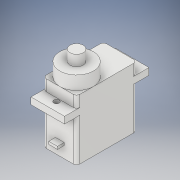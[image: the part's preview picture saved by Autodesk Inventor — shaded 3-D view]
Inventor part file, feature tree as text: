
AUTODESK INVENTOR PART (.ipt)
format: ipt  version: 2018 (Build 220112000, 112)  size: 165,376 bytes
history: native  units: in
note: dims shown in document units (in); Inventor stores cm internally (conversion verified against a paired STEP export)
features: extrude x5, sketch x5, plane x1
ambient origin geometry x8: Origin, YZ Plane, XZ Plane, XY Plane, X Axis, Y Axis, Z Axis, Center Point
bodies: Solid1 (feature_tree)
feature tree (11):
  extrude  "Extrusion1"  Depth=0.9in
  extrude  "Extrusion2"  Depth=0.9in TaperAngle=0.0deg
  plane  "Work Plane1"
  extrude  "Extrusion4"  [1 undecoded]
  extrude  "Extrusion5"  Depth=0.08in
  extrude  "Extrusion6"  Depth=0.1in TaperAngle=0.0deg
  sketch  "Sketch1"  dims[d0=0.5in d1=0.9in]
  sketch  "Sketch2"  dims[d2=0.05in d3=0.9in d4=0.0in]
  sketch  "Sketch5"  dims[d7=0.2in d8=0.0in d12=-0.17in]
  sketch  "Sketch6"  dims[d13=0.63in d14=0.08in]
  sketch  "Sketch7"  dims[d15=1.0in d16=0.1in d17=0.0in d18=0.13in d19=0.04in d20=0.17in d21=0.1in d22=0.0in d23=0.1969in d24=0.16in d25=0.0in]
note: 1 required parameter value undecoded (feature->parameter linkage not recoverable at this tier; creation-order binding heuristic only, values carry confidence <= 0.55)
